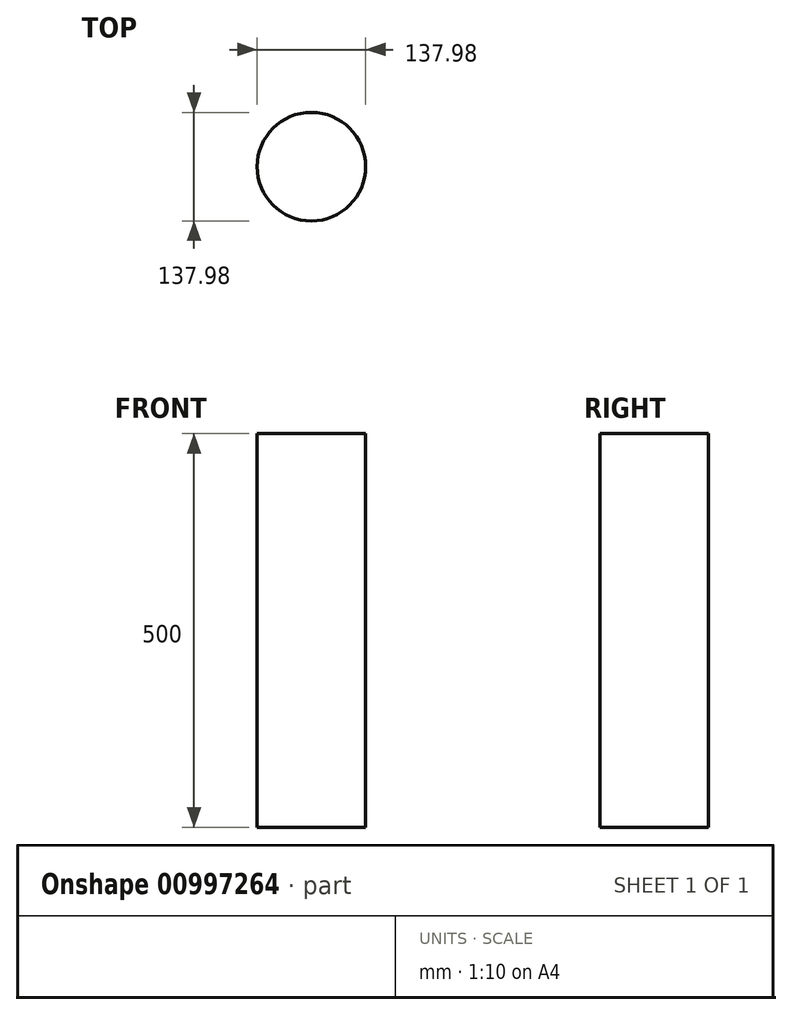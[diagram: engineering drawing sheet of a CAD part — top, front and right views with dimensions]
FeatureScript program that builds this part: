
annotation { "Feature Type Name" : "Feature", "Feature Type Description" : "" }
export const myFeature = defineFeature(function(context is Context, id is Id, definition is map)
    precondition{}
    {
        {
            var Q0;
            Q0=qCreatedBy(makeId("Top.planeOp"),FACE);
            var sketch = newSketch(context, id + "F0", { "sketchPlane" : qUnion([Q0])});
            skCircle(sketch, "E0", {"center": v(0, 0) * mm, "radius": 68.99 * mm});
            skSolve(sketch);
        }
        {
            var Q0;
            Q0=makeQuery(id+"F0.imprint","IMPRINT",FACE,{"disambiguationData":[TD([[makeQuery(id+"F0.imprint","IMPRINT",EDGE,{"derivedFrom":sQuery(id+"F0.wireOp",EDGE,"E0")}),1.0]])]});
            extrude(context, id + "F1", {"entities" : qUnion([Q0]), "depth" : 500 * mm, "offsetDistance" : 25.4 * mm});
        }
    });
